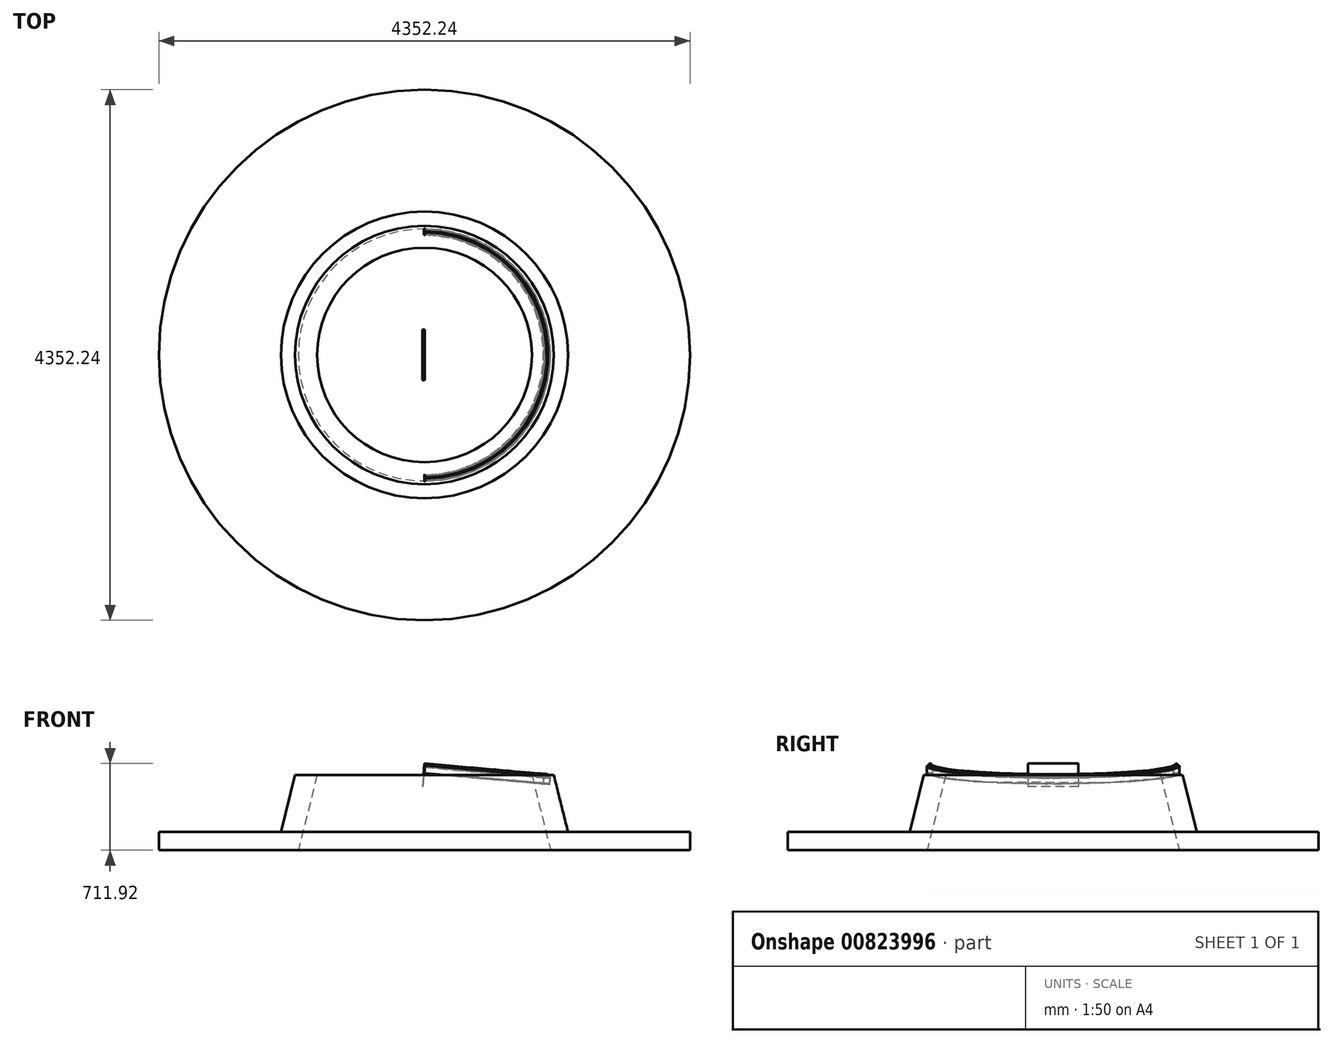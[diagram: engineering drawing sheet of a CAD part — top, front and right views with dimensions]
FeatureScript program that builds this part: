
annotation { "Feature Type Name" : "Feature", "Feature Type Description" : "" }
export const myFeature = defineFeature(function(context is Context, id is Id, definition is map)
    precondition{}
    {
        {
            var Q0;
            Q0=qCreatedBy(makeId("Front.planeOp"),FACE);
            var sketch = newSketch(context, id + "F0", { "sketchPlane" : qUnion([Q0])});
            skLineSegment(sketch, "E0", {"start": v(-2176.12, -465.74) * mm, "end": v(-1176.12, -465.74) * mm});
            skLineSegment(sketch, "E1", {"start": v(-1176.12, -465.74) * mm, "end": v(-1060, 0) * mm});
            skLineSegment(sketch, "E2", {"start": v(-1060, 0) * mm, "end": v(-880, 0) * mm});
            skLineSegment(sketch, "E3", {"start": v(-880, 0) * mm, "end": v(-1033.52, -615.74) * mm});
            skLineSegment(sketch, "E4", {"start": v(-2176.12, -465.74) * mm, "end": v(-2176.12, -615.74) * mm});
            skLineSegment(sketch, "E5", {"start": v(-2176.12, -615.74) * mm, "end": v(-1033.52, -615.74) * mm});
            skLineSegment(sketch, "E6", {"start": v(0, 0) * mm, "end": v(0, -606.45) * mm});
            skSolve(sketch);
        }
        {
            var Q0;
            Q0 = qSketchRegion(id + "F0", true);
            var Q1;
            Q1=sQuery(id+"F0.wireOp",EDGE,"E6");
            revolve(context, id + "F1", {"surfaceOperationType" : NewSurfaceOperationType.NEW, "entities" : qUnion([Q0]), "axis" : qUnion([Q1]), "revolveType" : RevolveType.FULL});
        }
        {
            var Q0;
            Q0=qCreatedBy(makeId("Right.planeOp"),FACE);
            var sketch = newSketch(context, id + "F2", { "sketchPlane" : qUnion([Q0])});
            skLineSegment(sketch, "E7.bottom", {"start": v(207.66, 95.39) * mm, "end": v(-207.66, 95.39) * mm});
            skLineSegment(sketch, "E7.top", {"start": v(207.66, -95.39) * mm, "end": v(-207.66, -95.39) * mm});
            skLineSegment(sketch, "E7.left", {"start": v(207.66, 95.39) * mm, "end": v(207.66, -95.39) * mm});
            skLineSegment(sketch, "E7.right", {"start": v(-207.66, 95.39) * mm, "end": v(-207.66, -95.39) * mm});
            skPoint(sketch, "E7.middle", {"position": v(0, 0) * mm});
            skSolve(sketch);
        }
        {
            var Q0;
            Q0=makeQuery(id+"F2.imprint","IMPRINT",FACE,{"disambiguationData":[TD([[makeQuery(id+"F2.imprint","IMPRINT",EDGE,{"derivedFrom":sQuery(id+"F2.wireOp",EDGE,"E7.bottom")}),1.0]])]});
            extrude(context, id + "F3", {"entities" : qUnion([Q0]), "depth" : 2 * mm, "offsetDistance" : 25 * mm});
        }
        {
            var Q0;
            Q0=makeQuery(id+"F3.opExtrude","SWEPT_BODY",BODY,{"disambiguationData":[OSD([sQuery(id+"F2.wireOp",EDGE,"E7.bottom"),sQuery(id+"F2.wireOp",EDGE,"E7.top"),sQuery(id+"F2.wireOp",EDGE,"E7.left"),sQuery(id+"F2.wireOp",EDGE,"E7.right")])]});
            var Q1;
            Q1=sQuery(id+"F2.wireOp",EDGE,"E7.bottom");
            transform(context, id + "F4", {"entities" : qUnion([Q0]), "transformType" : TransformType.ROTATION, "transformAxis" : qUnion([Q1]), "angle" : 5 * degree, "oppositeDirection" : true, "makeCopy" : false});
        }
        {
            var Q0;
            Q0=makeQuery(id+"F3.opExtrude","CAP_FACE",FACE,{"disambiguationData":[OSD([sQuery(id+"F2.wireOp",EDGE,"E7.bottom"),sQuery(id+"F2.wireOp",EDGE,"E7.top"),sQuery(id+"F2.wireOp",EDGE,"E7.left"),sQuery(id+"F2.wireOp",EDGE,"E7.right")])],"isStart":false});
            var sketch = newSketch(context, id + "F5", { "sketchPlane" : qUnion([Q0])});
            skArc(sketch, "E8", {"start": v(1012, 66) * mm, "mid": v(1012.7, 66.3) * mm, "end": v(1013, 67) * mm});
            skLineSegment(sketch, "E9", {"start": v(1013, 67) * mm, "end": v(1013, 78) * mm});
            skArc(sketch, "E10", {"start": v(1013, 78) * mm, "mid": v(1012.7, 78.7) * mm, "end": v(1012, 79) * mm});
            skLineSegment(sketch, "E11", {"start": v(1012, 79) * mm, "end": v(1008, 79) * mm});
            skArc(sketch, "E12", {"start": v(1008, 79) * mm, "mid": v(1007.3, 78.7) * mm, "end": v(1007, 78) * mm});
            skLineSegment(sketch, "E13", {"start": v(1007, 78) * mm, "end": v(1007, 67) * mm});
            skArc(sketch, "E14", {"start": v(1007, 67) * mm, "mid": v(1007.3, 66.3) * mm, "end": v(1008, 66) * mm});
            skLineSegment(sketch, "E15", {"start": v(1008, 66) * mm, "end": v(1012, 66) * mm});
            skLineSegment(sketch, "E16", {"start": v(986.6, 18.5) * mm, "end": v(995.5, 18.5) * mm});
            skLineSegment(sketch, "E17", {"start": v(995.5, 18.5) * mm, "end": v(995.5, 20.2) * mm});
            skLineSegment(sketch, "E18", {"start": v(995.5, 20.2) * mm, "end": v(997, 20.2) * mm});
            skLineSegment(sketch, "E19", {"start": v(997, 20.2) * mm, "end": v(997, 18.5) * mm});
            skLineSegment(sketch, "E20", {"start": v(997, 18.5) * mm, "end": v(1023, 18.5) * mm});
            skLineSegment(sketch, "E21", {"start": v(1023, 18.5) * mm, "end": v(1023, 20.2) * mm});
            skLineSegment(sketch, "E22", {"start": v(1023, 20.2) * mm, "end": v(1024.5, 20.2) * mm});
            skLineSegment(sketch, "E23", {"start": v(1024.5, 20.2) * mm, "end": v(1024.5, 18.5) * mm});
            skLineSegment(sketch, "E24", {"start": v(1024.5, 18.5) * mm, "end": v(1033.4, 18.5) * mm});
            skArc(sketch, "E25", {"start": v(1033.4, 18.5) * mm, "mid": v(1033.75, 18.65) * mm, "end": v(1033.9, 19) * mm});
            skLineSegment(sketch, "E26", {"start": v(1033.9, 19) * mm, "end": v(1033.9, 63.2) * mm});
            skArc(sketch, "E27", {"start": v(1033.9, 63.2) * mm, "mid": v(1033.75, 63.55) * mm, "end": v(1033.4, 63.7) * mm});
            skLineSegment(sketch, "E28", {"start": v(1033.4, 63.7) * mm, "end": v(986.6, 63.7) * mm});
            skArc(sketch, "E29", {"start": v(986.6, 63.7) * mm, "mid": v(986.25, 63.55) * mm, "end": v(986.1, 63.2) * mm});
            skLineSegment(sketch, "E30", {"start": v(986.1, 63.2) * mm, "end": v(986.1, 19) * mm});
            skArc(sketch, "E31", {"start": v(986.1, 19) * mm, "mid": v(986.25, 18.65) * mm, "end": v(986.6, 18.5) * mm});
            skArc(sketch, "E32", {"start": v(987.2, 67.35) * mm, "mid": v(988.85, 66) * mm, "end": v(990.31, 67.56) * mm});
            skLineSegment(sketch, "E33", {"start": v(990.3, 67.56) * mm, "end": v(990.3, 68.02) * mm});
            skArc(sketch, "E34", {"start": v(990.3, 68.02) * mm, "mid": v(990.35, 68.17) * mm, "end": v(990.46, 68.28) * mm});
            skLineSegment(sketch, "E35", {"start": v(990.46, 68.28) * mm, "end": v(990.6, 68.37) * mm});
            skArc(sketch, "E36", {"start": v(990.61, 68.37) * mm, "mid": v(990.7, 68.54) * mm, "end": v(990.61, 68.71) * mm});
            skLineSegment(sketch, "E37", {"start": v(990.6, 68.71) * mm, "end": v(990.46, 68.8) * mm});
            skArc(sketch, "E38", {"start": v(990.46, 68.8) * mm, "mid": v(990.35, 68.91) * mm, "end": v(990.3, 69.06) * mm});
            skLineSegment(sketch, "E39", {"start": v(990.3, 69.06) * mm, "end": v(990.3, 69.42) * mm});
            skArc(sketch, "E40", {"start": v(990.3, 69.42) * mm, "mid": v(990.35, 69.57) * mm, "end": v(990.46, 69.68) * mm});
            skLineSegment(sketch, "E41", {"start": v(990.46, 69.68) * mm, "end": v(990.6, 69.77) * mm});
            skArc(sketch, "E42", {"start": v(990.61, 69.77) * mm, "mid": v(990.7, 69.94) * mm, "end": v(990.61, 70.11) * mm});
            skLineSegment(sketch, "E43", {"start": v(990.6, 70.11) * mm, "end": v(990.46, 70.2) * mm});
            skArc(sketch, "E44", {"start": v(990.46, 70.2) * mm, "mid": v(990.45, 70.2) * mm, "end": v(990.45, 70.2) * mm});
            skLineSegment(sketch, "E45", {"start": v(990.45, 70.2) * mm, "end": v(991.3, 71.07) * mm});
            skLineSegment(sketch, "E46", {"start": v(991.3, 71.07) * mm, "end": v(991.3, 72) * mm});
            skLineSegment(sketch, "E47", {"start": v(991.3, 72) * mm, "end": v(990.3, 72) * mm});
            skLineSegment(sketch, "E48", {"start": v(990.3, 72) * mm, "end": v(990.3, 72.22) * mm});
            skArc(sketch, "E49", {"start": v(990.3, 72.22) * mm, "mid": v(990.35, 72.37) * mm, "end": v(990.46, 72.48) * mm});
            skLineSegment(sketch, "E50", {"start": v(990.46, 72.48) * mm, "end": v(990.6, 72.57) * mm});
            skArc(sketch, "E51", {"start": v(990.61, 72.57) * mm, "mid": v(990.7, 72.74) * mm, "end": v(990.61, 72.91) * mm});
            skLineSegment(sketch, "E52", {"start": v(990.6, 72.91) * mm, "end": v(990.46, 73) * mm});
            skArc(sketch, "E53", {"start": v(990.46, 73) * mm, "mid": v(990.35, 73.11) * mm, "end": v(990.3, 73.26) * mm});
            skLineSegment(sketch, "E54", {"start": v(990.3, 73.26) * mm, "end": v(990.3, 73.62) * mm});
            skArc(sketch, "E55", {"start": v(990.3, 73.62) * mm, "mid": v(990.35, 73.77) * mm, "end": v(990.46, 73.88) * mm});
            skLineSegment(sketch, "E56", {"start": v(990.46, 73.88) * mm, "end": v(990.6, 73.97) * mm});
            skArc(sketch, "E57", {"start": v(990.61, 73.97) * mm, "mid": v(990.7, 74.14) * mm, "end": v(990.61, 74.31) * mm});
            skLineSegment(sketch, "E58", {"start": v(990.6, 74.31) * mm, "end": v(990.46, 74.4) * mm});
            skArc(sketch, "E59", {"start": v(990.46, 74.4) * mm, "mid": v(990.35, 74.51) * mm, "end": v(990.3, 74.66) * mm});
            skLineSegment(sketch, "E60", {"start": v(990.3, 74.66) * mm, "end": v(990.3, 75.02) * mm});
            skArc(sketch, "E61", {"start": v(990.3, 75.02) * mm, "mid": v(990.35, 75.17) * mm, "end": v(990.46, 75.28) * mm});
            skLineSegment(sketch, "E62", {"start": v(990.46, 75.28) * mm, "end": v(990.6, 75.37) * mm});
            skArc(sketch, "E63", {"start": v(990.61, 75.37) * mm, "mid": v(990.7, 75.54) * mm, "end": v(990.61, 75.71) * mm});
            skLineSegment(sketch, "E64", {"start": v(990.6, 75.71) * mm, "end": v(990.46, 75.8) * mm});
            skArc(sketch, "E65", {"start": v(990.46, 75.8) * mm, "mid": v(990.35, 75.91) * mm, "end": v(990.31, 76.07) * mm});
            skLineSegment(sketch, "E66", {"start": v(990.31, 76.07) * mm, "end": v(991.3, 77.07) * mm});
            skLineSegment(sketch, "E67", {"start": v(991.3, 77.07) * mm, "end": v(991.3, 78) * mm});
            skLineSegment(sketch, "E68", {"start": v(991.3, 78) * mm, "end": v(990.3, 78) * mm});
            skLineSegment(sketch, "E69", {"start": v(990.3, 78) * mm, "end": v(990.3, 78.5) * mm});
            skLineSegment(sketch, "E70", {"start": v(990.3, 78.5) * mm, "end": v(990.8, 79) * mm});
            skLineSegment(sketch, "E71", {"start": v(990.8, 79) * mm, "end": v(993.5, 79) * mm});
            skLineSegment(sketch, "E72", {"start": v(993.5, 79) * mm, "end": v(993.5, 67) * mm});
            skArc(sketch, "E73", {"start": v(993.5, 67) * mm, "mid": v(993.8, 66.3) * mm, "end": v(994.5, 66) * mm});
            skLineSegment(sketch, "E74", {"start": v(994.5, 66) * mm, "end": v(998.95, 66) * mm});
            skLineSegment(sketch, "E75", {"start": v(998.95, 66) * mm, "end": v(999.25, 65.7) * mm});
            skLineSegment(sketch, "E76", {"start": v(999.25, 65.7) * mm, "end": v(999.55, 66) * mm});
            skLineSegment(sketch, "E77", {"start": v(999.55, 66) * mm, "end": v(1004, 66) * mm});
            skArc(sketch, "E78", {"start": v(1004, 66) * mm, "mid": v(1004.7, 66.3) * mm, "end": v(1005, 67) * mm});
            skLineSegment(sketch, "E79", {"start": v(1005, 67) * mm, "end": v(1005, 96) * mm});
            skLineSegment(sketch, "E80", {"start": v(1005, 96) * mm, "end": v(1006.7, 96) * mm});
            skLineSegment(sketch, "E81", {"start": v(1006.7, 96) * mm, "end": v(1007.88, 94.82) * mm});
            skArc(sketch, "E82", {"start": v(1007.88, 94.82) * mm, "mid": v(1007.88, 94.61) * mm, "end": v(1007.75, 94.46) * mm});
            skLineSegment(sketch, "E83", {"start": v(1007.75, 94.46) * mm, "end": v(1007.6, 94.37) * mm});
            skArc(sketch, "E84", {"start": v(1007.6, 94.37) * mm, "mid": v(1007.5, 94.2) * mm, "end": v(1007.6, 94.03) * mm});
            skLineSegment(sketch, "E85", {"start": v(1007.6, 94.03) * mm, "end": v(1007.75, 93.94) * mm});
            skArc(sketch, "E86", {"start": v(1007.75, 93.94) * mm, "mid": v(1007.86, 93.83) * mm, "end": v(1007.9, 93.68) * mm});
            skLineSegment(sketch, "E87", {"start": v(1007.9, 93.68) * mm, "end": v(1007.9, 92.92) * mm});
            skArc(sketch, "E88", {"start": v(1007.9, 92.92) * mm, "mid": v(1007.86, 92.77) * mm, "end": v(1007.75, 92.66) * mm});
            skLineSegment(sketch, "E89", {"start": v(1007.75, 92.66) * mm, "end": v(1007.6, 92.57) * mm});
            skArc(sketch, "E90", {"start": v(1007.6, 92.57) * mm, "mid": v(1007.5, 92.4) * mm, "end": v(1007.6, 92.23) * mm});
            skLineSegment(sketch, "E91", {"start": v(1007.6, 92.23) * mm, "end": v(1007.75, 92.14) * mm});
            skArc(sketch, "E92", {"start": v(1007.75, 92.14) * mm, "mid": v(1007.86, 92.03) * mm, "end": v(1007.9, 91.88) * mm});
            skLineSegment(sketch, "E93", {"start": v(1007.9, 91.88) * mm, "end": v(1007.9, 91.12) * mm});
            skArc(sketch, "E94", {"start": v(1007.9, 91.12) * mm, "mid": v(1007.86, 90.97) * mm, "end": v(1007.75, 90.86) * mm});
            skLineSegment(sketch, "E95", {"start": v(1007.75, 90.86) * mm, "end": v(1007.6, 90.77) * mm});
            skArc(sketch, "E96", {"start": v(1007.6, 90.77) * mm, "mid": v(1007.5, 90.6) * mm, "end": v(1007.6, 90.43) * mm});
            skLineSegment(sketch, "E97", {"start": v(1007.6, 90.43) * mm, "end": v(1007.75, 90.34) * mm});
            skArc(sketch, "E98", {"start": v(1007.75, 90.34) * mm, "mid": v(1007.86, 90.23) * mm, "end": v(1007.9, 90.08) * mm});
            skLineSegment(sketch, "E99", {"start": v(1007.9, 90.08) * mm, "end": v(1007.9, 89.32) * mm});
            skArc(sketch, "E100", {"start": v(1007.9, 89.32) * mm, "mid": v(1007.86, 89.17) * mm, "end": v(1007.75, 89.06) * mm});
            skLineSegment(sketch, "E101", {"start": v(1007.75, 89.06) * mm, "end": v(1007.6, 88.97) * mm});
            skArc(sketch, "E102", {"start": v(1007.6, 88.97) * mm, "mid": v(1007.5, 88.8) * mm, "end": v(1007.6, 88.63) * mm});
            skLineSegment(sketch, "E103", {"start": v(1007.6, 88.63) * mm, "end": v(1007.75, 88.54) * mm});
            skArc(sketch, "E104", {"start": v(1007.75, 88.54) * mm, "mid": v(1007.86, 88.43) * mm, "end": v(1007.9, 88.28) * mm});
            skLineSegment(sketch, "E105", {"start": v(1007.9, 88.28) * mm, "end": v(1007.9, 87.52) * mm});
            skArc(sketch, "E106", {"start": v(1007.9, 87.52) * mm, "mid": v(1007.86, 87.37) * mm, "end": v(1007.75, 87.26) * mm});
            skLineSegment(sketch, "E107", {"start": v(1007.75, 87.26) * mm, "end": v(1007.6, 87.17) * mm});
            skArc(sketch, "E108", {"start": v(1007.6, 87.17) * mm, "mid": v(1007.5, 87) * mm, "end": v(1007.6, 86.83) * mm});
            skLineSegment(sketch, "E109", {"start": v(1007.6, 86.83) * mm, "end": v(1007.75, 86.74) * mm});
            skArc(sketch, "E110", {"start": v(1007.75, 86.74) * mm, "mid": v(1007.86, 86.63) * mm, "end": v(1007.9, 86.48) * mm});
            skLineSegment(sketch, "E111", {"start": v(1007.9, 86.48) * mm, "end": v(1007.9, 85.72) * mm});
            skArc(sketch, "E112", {"start": v(1007.9, 85.72) * mm, "mid": v(1007.86, 85.57) * mm, "end": v(1007.75, 85.46) * mm});
            skLineSegment(sketch, "E113", {"start": v(1007.75, 85.46) * mm, "end": v(1007.6, 85.37) * mm});
            skArc(sketch, "E114", {"start": v(1007.6, 85.37) * mm, "mid": v(1007.5, 85.2) * mm, "end": v(1007.6, 85.03) * mm});
            skLineSegment(sketch, "E115", {"start": v(1007.6, 85.03) * mm, "end": v(1007.75, 84.94) * mm});
            skArc(sketch, "E116", {"start": v(1007.75, 84.94) * mm, "mid": v(1007.86, 84.83) * mm, "end": v(1007.9, 84.68) * mm});
            skLineSegment(sketch, "E117", {"start": v(1007.9, 84.68) * mm, "end": v(1007.9, 83.1) * mm});
            skArc(sketch, "E118", {"start": v(1007.9, 83.1) * mm, "mid": v(1008.34, 82.04) * mm, "end": v(1009.4, 81.6) * mm});
            skLineSegment(sketch, "E119", {"start": v(1009.4, 81.6) * mm, "end": v(1010.6, 81.6) * mm});
            skArc(sketch, "E120", {"start": v(1010.6, 81.6) * mm, "mid": v(1011.66, 82.04) * mm, "end": v(1012.1, 83.1) * mm});
            skLineSegment(sketch, "E121", {"start": v(1012.1, 83.1) * mm, "end": v(1012.1, 83.78) * mm});
            skArc(sketch, "E122", {"start": v(1012.1, 83.78) * mm, "mid": v(1012.14, 83.93) * mm, "end": v(1012.25, 84.04) * mm});
            skLineSegment(sketch, "E123", {"start": v(1012.25, 84.04) * mm, "end": v(1012.4, 84.13) * mm});
            skArc(sketch, "E124", {"start": v(1012.4, 84.13) * mm, "mid": v(1012.5, 84.3) * mm, "end": v(1012.4, 84.47) * mm});
            skLineSegment(sketch, "E125", {"start": v(1012.4, 84.47) * mm, "end": v(1012.25, 84.56) * mm});
            skArc(sketch, "E126", {"start": v(1012.25, 84.56) * mm, "mid": v(1012.14, 84.67) * mm, "end": v(1012.1, 84.82) * mm});
            skLineSegment(sketch, "E127", {"start": v(1012.1, 84.82) * mm, "end": v(1012.1, 85.58) * mm});
            skArc(sketch, "E128", {"start": v(1012.1, 85.58) * mm, "mid": v(1012.14, 85.73) * mm, "end": v(1012.25, 85.84) * mm});
            skLineSegment(sketch, "E129", {"start": v(1012.25, 85.84) * mm, "end": v(1012.4, 85.93) * mm});
            skArc(sketch, "E130", {"start": v(1012.4, 85.93) * mm, "mid": v(1012.5, 86.1) * mm, "end": v(1012.4, 86.27) * mm});
            skLineSegment(sketch, "E131", {"start": v(1012.4, 86.27) * mm, "end": v(1012.25, 86.36) * mm});
            skArc(sketch, "E132", {"start": v(1012.25, 86.36) * mm, "mid": v(1012.14, 86.47) * mm, "end": v(1012.1, 86.62) * mm});
            skLineSegment(sketch, "E133", {"start": v(1012.1, 86.62) * mm, "end": v(1012.1, 87.38) * mm});
            skArc(sketch, "E134", {"start": v(1012.1, 87.38) * mm, "mid": v(1012.14, 87.53) * mm, "end": v(1012.25, 87.64) * mm});
            skLineSegment(sketch, "E135", {"start": v(1012.25, 87.64) * mm, "end": v(1012.4, 87.73) * mm});
            skArc(sketch, "E136", {"start": v(1012.4, 87.73) * mm, "mid": v(1012.5, 87.9) * mm, "end": v(1012.4, 88.07) * mm});
            skLineSegment(sketch, "E137", {"start": v(1012.4, 88.07) * mm, "end": v(1012.25, 88.16) * mm});
            skArc(sketch, "E138", {"start": v(1012.25, 88.16) * mm, "mid": v(1012.14, 88.27) * mm, "end": v(1012.1, 88.42) * mm});
            skLineSegment(sketch, "E139", {"start": v(1012.1, 88.42) * mm, "end": v(1012.1, 89.18) * mm});
            skArc(sketch, "E140", {"start": v(1012.1, 89.18) * mm, "mid": v(1012.14, 89.33) * mm, "end": v(1012.25, 89.44) * mm});
            skLineSegment(sketch, "E141", {"start": v(1012.25, 89.44) * mm, "end": v(1012.4, 89.53) * mm});
            skArc(sketch, "E142", {"start": v(1012.4, 89.53) * mm, "mid": v(1012.5, 89.7) * mm, "end": v(1012.4, 89.87) * mm});
            skLineSegment(sketch, "E143", {"start": v(1012.4, 89.87) * mm, "end": v(1012.25, 89.96) * mm});
            skArc(sketch, "E144", {"start": v(1012.25, 89.96) * mm, "mid": v(1012.14, 90.07) * mm, "end": v(1012.1, 90.22) * mm});
            skLineSegment(sketch, "E145", {"start": v(1012.1, 90.22) * mm, "end": v(1012.1, 90.98) * mm});
            skArc(sketch, "E146", {"start": v(1012.1, 90.98) * mm, "mid": v(1012.14, 91.13) * mm, "end": v(1012.25, 91.24) * mm});
            skLineSegment(sketch, "E147", {"start": v(1012.25, 91.24) * mm, "end": v(1012.4, 91.33) * mm});
            skArc(sketch, "E148", {"start": v(1012.4, 91.33) * mm, "mid": v(1012.5, 91.5) * mm, "end": v(1012.4, 91.67) * mm});
            skLineSegment(sketch, "E149", {"start": v(1012.4, 91.67) * mm, "end": v(1012.25, 91.76) * mm});
            skArc(sketch, "E150", {"start": v(1012.25, 91.76) * mm, "mid": v(1012.14, 91.87) * mm, "end": v(1012.1, 92.02) * mm});
            skLineSegment(sketch, "E151", {"start": v(1012.1, 92.02) * mm, "end": v(1012.1, 92.78) * mm});
            skArc(sketch, "E152", {"start": v(1012.1, 92.78) * mm, "mid": v(1012.14, 92.93) * mm, "end": v(1012.25, 93.04) * mm});
            skLineSegment(sketch, "E153", {"start": v(1012.25, 93.04) * mm, "end": v(1012.4, 93.13) * mm});
            skArc(sketch, "E154", {"start": v(1012.4, 93.13) * mm, "mid": v(1012.5, 93.3) * mm, "end": v(1012.4, 93.47) * mm});
            skLineSegment(sketch, "E155", {"start": v(1012.4, 93.47) * mm, "end": v(1012.25, 93.56) * mm});
            skArc(sketch, "E156", {"start": v(1012.25, 93.56) * mm, "mid": v(1012.14, 93.67) * mm, "end": v(1012.1, 93.82) * mm});
            skLineSegment(sketch, "E157", {"start": v(1012.1, 93.82) * mm, "end": v(1012.1, 94.8) * mm});
            skLineSegment(sketch, "E158", {"start": v(1012.1, 94.8) * mm, "end": v(1013.3, 96) * mm});
            skLineSegment(sketch, "E159", {"start": v(1013.3, 96) * mm, "end": v(1015, 96) * mm});
            skLineSegment(sketch, "E160", {"start": v(1015, 96) * mm, "end": v(1015, 67) * mm});
            skArc(sketch, "E161", {"start": v(1015, 67) * mm, "mid": v(1015.3, 66.3) * mm, "end": v(1016, 66) * mm});
            skLineSegment(sketch, "E162", {"start": v(1016, 66) * mm, "end": v(1020.45, 66) * mm});
            skLineSegment(sketch, "E163", {"start": v(1020.45, 66) * mm, "end": v(1020.75, 65.7) * mm});
            skLineSegment(sketch, "E164", {"start": v(1020.75, 65.7) * mm, "end": v(1021.05, 66) * mm});
            skLineSegment(sketch, "E165", {"start": v(1021.05, 66) * mm, "end": v(1025.5, 66) * mm});
            skArc(sketch, "E166", {"start": v(1025.5, 66) * mm, "mid": v(1026.2, 66.3) * mm, "end": v(1026.5, 67) * mm});
            skLineSegment(sketch, "E167", {"start": v(1026.5, 67) * mm, "end": v(1026.5, 79) * mm});
            skLineSegment(sketch, "E168", {"start": v(1026.5, 79) * mm, "end": v(1029.19, 79) * mm});
            skLineSegment(sketch, "E169", {"start": v(1029.19, 79) * mm, "end": v(1029.69, 78.5) * mm});
            skLineSegment(sketch, "E170", {"start": v(1029.69, 78.5) * mm, "end": v(1029.69, 78) * mm});
            skLineSegment(sketch, "E171", {"start": v(1029.69, 78) * mm, "end": v(1028.69, 78) * mm});
            skLineSegment(sketch, "E172", {"start": v(1028.69, 78) * mm, "end": v(1028.69, 77.07) * mm});
            skLineSegment(sketch, "E173", {"start": v(1028.69, 77.07) * mm, "end": v(1029.69, 76.07) * mm});
            skArc(sketch, "E174", {"start": v(1029.69, 76.07) * mm, "mid": v(1029.65, 75.91) * mm, "end": v(1029.54, 75.8) * mm});
            skLineSegment(sketch, "E175", {"start": v(1029.54, 75.8) * mm, "end": v(1029.39, 75.71) * mm});
            skArc(sketch, "E176", {"start": v(1029.39, 75.71) * mm, "mid": v(1029.29, 75.54) * mm, "end": v(1029.39, 75.37) * mm});
            skLineSegment(sketch, "E177", {"start": v(1029.39, 75.37) * mm, "end": v(1029.54, 75.28) * mm});
            skArc(sketch, "E178", {"start": v(1029.54, 75.28) * mm, "mid": v(1029.65, 75.17) * mm, "end": v(1029.69, 75.02) * mm});
            skLineSegment(sketch, "E179", {"start": v(1029.69, 75.02) * mm, "end": v(1029.69, 74.66) * mm});
            skArc(sketch, "E180", {"start": v(1029.69, 74.66) * mm, "mid": v(1029.65, 74.51) * mm, "end": v(1029.54, 74.4) * mm});
            skLineSegment(sketch, "E181", {"start": v(1029.54, 74.4) * mm, "end": v(1029.39, 74.31) * mm});
            skArc(sketch, "E182", {"start": v(1029.39, 74.31) * mm, "mid": v(1029.29, 74.14) * mm, "end": v(1029.39, 73.97) * mm});
            skLineSegment(sketch, "E183", {"start": v(1029.39, 73.97) * mm, "end": v(1029.54, 73.88) * mm});
            skArc(sketch, "E184", {"start": v(1029.54, 73.88) * mm, "mid": v(1029.65, 73.77) * mm, "end": v(1029.69, 73.62) * mm});
            skLineSegment(sketch, "E185", {"start": v(1029.69, 73.62) * mm, "end": v(1029.69, 73.26) * mm});
            skArc(sketch, "E186", {"start": v(1029.69, 73.26) * mm, "mid": v(1029.65, 73.11) * mm, "end": v(1029.54, 73) * mm});
            skLineSegment(sketch, "E187", {"start": v(1029.54, 73) * mm, "end": v(1029.39, 72.91) * mm});
            skArc(sketch, "E188", {"start": v(1029.39, 72.91) * mm, "mid": v(1029.29, 72.74) * mm, "end": v(1029.39, 72.57) * mm});
            skLineSegment(sketch, "E189", {"start": v(1029.39, 72.57) * mm, "end": v(1029.54, 72.48) * mm});
            skArc(sketch, "E190", {"start": v(1029.54, 72.48) * mm, "mid": v(1029.65, 72.37) * mm, "end": v(1029.69, 72.22) * mm});
            skLineSegment(sketch, "E191", {"start": v(1029.69, 72.22) * mm, "end": v(1029.69, 72) * mm});
            skLineSegment(sketch, "E192", {"start": v(1029.69, 72) * mm, "end": v(1028.69, 72) * mm});
            skLineSegment(sketch, "E193", {"start": v(1028.69, 72) * mm, "end": v(1028.69, 71.07) * mm});
            skLineSegment(sketch, "E194", {"start": v(1028.69, 71.07) * mm, "end": v(1029.55, 70.2) * mm});
            skArc(sketch, "E195", {"start": v(1029.55, 70.2) * mm, "mid": v(1029.55, 70.2) * mm, "end": v(1029.54, 70.2) * mm});
            skLineSegment(sketch, "E196", {"start": v(1029.54, 70.2) * mm, "end": v(1029.39, 70.11) * mm});
            skArc(sketch, "E197", {"start": v(1029.39, 70.11) * mm, "mid": v(1029.29, 69.94) * mm, "end": v(1029.39, 69.77) * mm});
            skLineSegment(sketch, "E198", {"start": v(1029.39, 69.77) * mm, "end": v(1029.54, 69.68) * mm});
            skArc(sketch, "E199", {"start": v(1029.54, 69.68) * mm, "mid": v(1029.65, 69.57) * mm, "end": v(1029.69, 69.42) * mm});
            skLineSegment(sketch, "E200", {"start": v(1029.69, 69.42) * mm, "end": v(1029.69, 69.06) * mm});
            skArc(sketch, "E201", {"start": v(1029.69, 69.06) * mm, "mid": v(1029.65, 68.91) * mm, "end": v(1029.54, 68.8) * mm});
            skLineSegment(sketch, "E202", {"start": v(1029.54, 68.8) * mm, "end": v(1029.39, 68.71) * mm});
            skArc(sketch, "E203", {"start": v(1029.39, 68.71) * mm, "mid": v(1029.29, 68.54) * mm, "end": v(1029.39, 68.37) * mm});
            skLineSegment(sketch, "E204", {"start": v(1029.39, 68.37) * mm, "end": v(1029.54, 68.28) * mm});
            skArc(sketch, "E205", {"start": v(1029.54, 68.28) * mm, "mid": v(1029.65, 68.17) * mm, "end": v(1029.69, 68.02) * mm});
            skLineSegment(sketch, "E206", {"start": v(1029.69, 68.02) * mm, "end": v(1029.69, 67.56) * mm});
            skArc(sketch, "E207", {"start": v(1029.7, 67.56) * mm, "mid": v(1031.15, 66) * mm, "end": v(1032.8, 67.35) * mm});
            skArc(sketch, "E208", {"start": v(1032.8, 67.35) * mm, "mid": v(1032.84, 67.48) * mm, "end": v(1032.94, 67.57) * mm});
            skLineSegment(sketch, "E209", {"start": v(1032.94, 67.57) * mm, "end": v(1033.1, 67.67) * mm});
            skArc(sketch, "E210", {"start": v(1033.11, 67.67) * mm, "mid": v(1033.2, 67.84) * mm, "end": v(1033.11, 68.01) * mm});
            skLineSegment(sketch, "E211", {"start": v(1033.1, 68.01) * mm, "end": v(1032.96, 68.1) * mm});
            skArc(sketch, "E212", {"start": v(1032.96, 68.1) * mm, "mid": v(1032.85, 68.21) * mm, "end": v(1032.8, 68.36) * mm});
            skLineSegment(sketch, "E213", {"start": v(1032.8, 68.36) * mm, "end": v(1032.8, 68.72) * mm});
            skArc(sketch, "E214", {"start": v(1032.8, 68.72) * mm, "mid": v(1032.85, 68.87) * mm, "end": v(1032.96, 68.98) * mm});
            skLineSegment(sketch, "E215", {"start": v(1032.96, 68.98) * mm, "end": v(1033.1, 69.07) * mm});
            skArc(sketch, "E216", {"start": v(1033.11, 69.07) * mm, "mid": v(1033.2, 69.24) * mm, "end": v(1033.11, 69.41) * mm});
            skLineSegment(sketch, "E217", {"start": v(1033.1, 69.41) * mm, "end": v(1032.96, 69.5) * mm});
            skArc(sketch, "E218", {"start": v(1032.96, 69.5) * mm, "mid": v(1032.85, 69.61) * mm, "end": v(1032.8, 69.76) * mm});
            skLineSegment(sketch, "E219", {"start": v(1032.8, 69.76) * mm, "end": v(1032.8, 70.07) * mm});
            skLineSegment(sketch, "E220", {"start": v(1032.8, 70.07) * mm, "end": v(1033.81, 71.07) * mm});
            skLineSegment(sketch, "E221", {"start": v(1033.8, 71.07) * mm, "end": v(1033.8, 72) * mm});
            skLineSegment(sketch, "E222", {"start": v(1033.8, 72) * mm, "end": v(1032.8, 72) * mm});
            skLineSegment(sketch, "E223", {"start": v(1032.8, 72) * mm, "end": v(1032.8, 72.92) * mm});
            skArc(sketch, "E224", {"start": v(1032.8, 72.92) * mm, "mid": v(1032.85, 73.07) * mm, "end": v(1032.96, 73.18) * mm});
            skLineSegment(sketch, "E225", {"start": v(1032.96, 73.18) * mm, "end": v(1033.1, 73.27) * mm});
            skArc(sketch, "E226", {"start": v(1033.11, 73.27) * mm, "mid": v(1033.2, 73.44) * mm, "end": v(1033.11, 73.61) * mm});
            skLineSegment(sketch, "E227", {"start": v(1033.1, 73.61) * mm, "end": v(1032.96, 73.7) * mm});
            skArc(sketch, "E228", {"start": v(1032.96, 73.7) * mm, "mid": v(1032.85, 73.81) * mm, "end": v(1032.8, 73.96) * mm});
            skLineSegment(sketch, "E229", {"start": v(1032.8, 73.96) * mm, "end": v(1032.8, 74.32) * mm});
            skArc(sketch, "E230", {"start": v(1032.8, 74.32) * mm, "mid": v(1032.85, 74.47) * mm, "end": v(1032.96, 74.58) * mm});
            skLineSegment(sketch, "E231", {"start": v(1032.96, 74.58) * mm, "end": v(1033.1, 74.67) * mm});
            skArc(sketch, "E232", {"start": v(1033.11, 74.67) * mm, "mid": v(1033.2, 74.84) * mm, "end": v(1033.11, 75.01) * mm});
            skLineSegment(sketch, "E233", {"start": v(1033.1, 75.01) * mm, "end": v(1032.96, 75.1) * mm});
            skArc(sketch, "E234", {"start": v(1032.96, 75.1) * mm, "mid": v(1032.85, 75.21) * mm, "end": v(1032.8, 75.36) * mm});
            skLineSegment(sketch, "E235", {"start": v(1032.8, 75.36) * mm, "end": v(1032.8, 76.07) * mm});
            skLineSegment(sketch, "E236", {"start": v(1032.8, 76.07) * mm, "end": v(1033.81, 77.07) * mm});
            skLineSegment(sketch, "E237", {"start": v(1033.8, 77.07) * mm, "end": v(1033.8, 78) * mm});
            skLineSegment(sketch, "E238", {"start": v(1033.8, 78) * mm, "end": v(1032.8, 78) * mm});
            skLineSegment(sketch, "E239", {"start": v(1032.8, 78) * mm, "end": v(1032.8, 78.5) * mm});
            skLineSegment(sketch, "E240", {"start": v(1032.8, 78.5) * mm, "end": v(1033.3, 79) * mm});
            skLineSegment(sketch, "E241", {"start": v(1033.3, 79) * mm, "end": v(1036, 79) * mm});
            skLineSegment(sketch, "E242", {"start": v(1036, 79) * mm, "end": v(1036, 14.5) * mm});
            skArc(sketch, "E243", {"start": v(1036, 14.5) * mm, "mid": v(1035.85, 14.15) * mm, "end": v(1035.5, 14) * mm});
            skLineSegment(sketch, "E244", {"start": v(1035.5, 14) * mm, "end": v(984.5, 14) * mm});
            skArc(sketch, "E245", {"start": v(984.5, 14) * mm, "mid": v(984.15, 14.15) * mm, "end": v(984, 14.5) * mm});
            skLineSegment(sketch, "E246", {"start": v(984, 14.5) * mm, "end": v(984, 79) * mm});
            skLineSegment(sketch, "E247", {"start": v(984, 79) * mm, "end": v(986.69, 79) * mm});
            skLineSegment(sketch, "E248", {"start": v(986.69, 79) * mm, "end": v(987.19, 78.5) * mm});
            skLineSegment(sketch, "E249", {"start": v(987.19, 78.5) * mm, "end": v(987.19, 78) * mm});
            skLineSegment(sketch, "E250", {"start": v(987.19, 78) * mm, "end": v(986.19, 78) * mm});
            skLineSegment(sketch, "E251", {"start": v(986.19, 78) * mm, "end": v(986.19, 77.07) * mm});
            skLineSegment(sketch, "E252", {"start": v(986.19, 77.07) * mm, "end": v(987.19, 76.07) * mm});
            skLineSegment(sketch, "E253", {"start": v(987.19, 76.07) * mm, "end": v(987.19, 75.36) * mm});
            skArc(sketch, "E254", {"start": v(987.19, 75.36) * mm, "mid": v(987.15, 75.21) * mm, "end": v(987.04, 75.1) * mm});
            skLineSegment(sketch, "E255", {"start": v(987.04, 75.1) * mm, "end": v(986.89, 75.01) * mm});
            skArc(sketch, "E256", {"start": v(986.89, 75.01) * mm, "mid": v(986.79, 74.84) * mm, "end": v(986.89, 74.67) * mm});
            skLineSegment(sketch, "E257", {"start": v(986.89, 74.67) * mm, "end": v(987.04, 74.58) * mm});
            skArc(sketch, "E258", {"start": v(987.04, 74.58) * mm, "mid": v(987.15, 74.47) * mm, "end": v(987.19, 74.32) * mm});
            skLineSegment(sketch, "E259", {"start": v(987.19, 74.32) * mm, "end": v(987.19, 73.96) * mm});
            skArc(sketch, "E260", {"start": v(987.19, 73.96) * mm, "mid": v(987.15, 73.81) * mm, "end": v(987.04, 73.7) * mm});
            skLineSegment(sketch, "E261", {"start": v(987.04, 73.7) * mm, "end": v(986.89, 73.61) * mm});
            skArc(sketch, "E262", {"start": v(986.89, 73.61) * mm, "mid": v(986.79, 73.44) * mm, "end": v(986.89, 73.27) * mm});
            skLineSegment(sketch, "E263", {"start": v(986.89, 73.27) * mm, "end": v(987.04, 73.18) * mm});
            skArc(sketch, "E264", {"start": v(987.04, 73.18) * mm, "mid": v(987.15, 73.07) * mm, "end": v(987.19, 72.92) * mm});
            skLineSegment(sketch, "E265", {"start": v(987.19, 72.92) * mm, "end": v(987.19, 72) * mm});
            skLineSegment(sketch, "E266", {"start": v(987.19, 72) * mm, "end": v(986.19, 72) * mm});
            skLineSegment(sketch, "E267", {"start": v(986.19, 72) * mm, "end": v(986.19, 71.07) * mm});
            skLineSegment(sketch, "E268", {"start": v(986.19, 71.07) * mm, "end": v(987.19, 70.07) * mm});
            skLineSegment(sketch, "E269", {"start": v(987.19, 70.07) * mm, "end": v(987.19, 69.76) * mm});
            skArc(sketch, "E270", {"start": v(987.19, 69.76) * mm, "mid": v(987.15, 69.61) * mm, "end": v(987.04, 69.5) * mm});
            skLineSegment(sketch, "E271", {"start": v(987.04, 69.5) * mm, "end": v(986.89, 69.41) * mm});
            skArc(sketch, "E272", {"start": v(986.89, 69.41) * mm, "mid": v(986.79, 69.24) * mm, "end": v(986.89, 69.07) * mm});
            skLineSegment(sketch, "E273", {"start": v(986.89, 69.07) * mm, "end": v(987.04, 68.98) * mm});
            skArc(sketch, "E274", {"start": v(987.04, 68.98) * mm, "mid": v(987.15, 68.87) * mm, "end": v(987.19, 68.72) * mm});
            skLineSegment(sketch, "E275", {"start": v(987.19, 68.72) * mm, "end": v(987.19, 68.36) * mm});
            skArc(sketch, "E276", {"start": v(987.19, 68.36) * mm, "mid": v(987.15, 68.21) * mm, "end": v(987.04, 68.1) * mm});
            skLineSegment(sketch, "E277", {"start": v(987.04, 68.1) * mm, "end": v(986.89, 68.01) * mm});
            skArc(sketch, "E278", {"start": v(986.89, 68.01) * mm, "mid": v(986.79, 67.84) * mm, "end": v(986.89, 67.67) * mm});
            skLineSegment(sketch, "E279", {"start": v(986.89, 67.67) * mm, "end": v(987.06, 67.57) * mm});
            skArc(sketch, "E280", {"start": v(987.06, 67.57) * mm, "mid": v(987.16, 67.48) * mm, "end": v(987.2, 67.35) * mm});
            skLineSegment(sketch, "E281", {"start": v(0, 0) * mm, "end": v(0, 95.02) * mm, "construction": true});
            skArc(sketch, "E282", {"start": v(1033.41, 83.26) * mm, "mid": v(1033.33, 83.05) * mm, "end": v(1033.11, 82.96) * mm});
            skLineSegment(sketch, "E283", {"start": v(1033.11, 82.96) * mm, "end": v(1029.41, 82.96) * mm});
            skArc(sketch, "E284", {"start": v(1029.41, 82.96) * mm, "mid": v(1029.2, 83.05) * mm, "end": v(1029.11, 83.26) * mm});
            skLineSegment(sketch, "E285", {"start": v(1029.11, 83.26) * mm, "end": v(1029.11, 85.47) * mm});
            skArc(sketch, "E286", {"start": v(1029.11, 85.47) * mm, "mid": v(1029.18, 85.66) * mm, "end": v(1029.35, 85.76) * mm});
            skLineSegment(sketch, "E287", {"start": v(1029.35, 85.76) * mm, "end": v(1031.26, 86.16) * mm});
            skLineSegment(sketch, "E288", {"start": v(1031.26, 86.16) * mm, "end": v(1033.18, 85.76) * mm});
            skArc(sketch, "E289", {"start": v(1033.18, 85.76) * mm, "mid": v(1033.35, 85.66) * mm, "end": v(1033.41, 85.47) * mm});
            skLineSegment(sketch, "E290", {"start": v(1033.41, 85.47) * mm, "end": v(1033.41, 83.26) * mm});
            skArc(sketch, "E291", {"start": v(1028.57, 79.76) * mm, "mid": v(1028.88, 79.82) * mm, "end": v(1029.14, 80) * mm});
            skLineSegment(sketch, "E292", {"start": v(1029.14, 80) * mm, "end": v(1029.52, 80.37) * mm});
            skArc(sketch, "E293", {"start": v(1029.52, 80.37) * mm, "mid": v(1029.61, 80.44) * mm, "end": v(1029.73, 80.46) * mm});
            skLineSegment(sketch, "E294", {"start": v(1029.73, 80.46) * mm, "end": v(1032.8, 80.46) * mm});
            skArc(sketch, "E295", {"start": v(1032.8, 80.46) * mm, "mid": v(1032.92, 80.44) * mm, "end": v(1033.01, 80.37) * mm});
            skLineSegment(sketch, "E296", {"start": v(1033.01, 80.37) * mm, "end": v(1033.4, 80) * mm});
            skArc(sketch, "E297", {"start": v(1033.4, 80) * mm, "mid": v(1033.65, 79.82) * mm, "end": v(1033.96, 79.76) * mm});
            skLineSegment(sketch, "E298", {"start": v(1033.96, 79.76) * mm, "end": v(1034.61, 79.76) * mm});
            skLineSegment(sketch, "E299", {"start": v(1034.61, 79.76) * mm, "end": v(1034.91, 80) * mm});
            skLineSegment(sketch, "E300", {"start": v(1034.91, 80) * mm, "end": v(1034.61, 80.26) * mm});
            skLineSegment(sketch, "E301", {"start": v(1034.61, 80.26) * mm, "end": v(1033.96, 80.26) * mm});
            skArc(sketch, "E302", {"start": v(1033.96, 80.26) * mm, "mid": v(1033.84, 80.28) * mm, "end": v(1033.74, 80.35) * mm});
            skLineSegment(sketch, "E303", {"start": v(1033.74, 80.35) * mm, "end": v(1033.37, 80.73) * mm});
            skArc(sketch, "E304", {"start": v(1033.37, 80.73) * mm, "mid": v(1033.1, 80.9) * mm, "end": v(1032.8, 80.96) * mm});
            skLineSegment(sketch, "E305", {"start": v(1032.8, 80.96) * mm, "end": v(1032.7, 80.6) * mm});
            skArc(sketch, "E306", {"start": v(1032.7, 80.6) * mm, "mid": v(1032.51, 80.46) * mm, "end": v(1032.32, 80.6) * mm});
            skLineSegment(sketch, "E307", {"start": v(1032.32, 80.6) * mm, "end": v(1032.23, 80.96) * mm});
            skLineSegment(sketch, "E308", {"start": v(1032.23, 80.96) * mm, "end": v(1030.3, 80.96) * mm});
            skLineSegment(sketch, "E309", {"start": v(1030.3, 80.96) * mm, "end": v(1030.2, 80.6) * mm});
            skArc(sketch, "E310", {"start": v(1030.2, 80.6) * mm, "mid": v(1030.02, 80.46) * mm, "end": v(1029.82, 80.6) * mm});
            skLineSegment(sketch, "E311", {"start": v(1029.82, 80.6) * mm, "end": v(1029.73, 80.96) * mm});
            skArc(sketch, "E312", {"start": v(1029.73, 80.96) * mm, "mid": v(1029.42, 80.9) * mm, "end": v(1029.16, 80.73) * mm});
            skLineSegment(sketch, "E313", {"start": v(1029.16, 80.73) * mm, "end": v(1028.79, 80.35) * mm});
            skArc(sketch, "E314", {"start": v(1028.79, 80.35) * mm, "mid": v(1028.69, 80.28) * mm, "end": v(1028.57, 80.26) * mm});
            skLineSegment(sketch, "E315", {"start": v(1028.57, 80.26) * mm, "end": v(1027.9, 80.26) * mm});
            skLineSegment(sketch, "E316", {"start": v(1027.9, 80.26) * mm, "end": v(1027.8, 79.9) * mm});
            skArc(sketch, "E317", {"start": v(1027.8, 79.9) * mm, "mid": v(1027.61, 79.76) * mm, "end": v(1027.42, 79.9) * mm});
            skLineSegment(sketch, "E318", {"start": v(1027.42, 79.9) * mm, "end": v(1027.33, 80.26) * mm});
            skLineSegment(sketch, "E319", {"start": v(1027.33, 80.26) * mm, "end": v(1026.81, 80.26) * mm});
            skArc(sketch, "E320", {"start": v(1026.81, 80.26) * mm, "mid": v(1026.6, 80.35) * mm, "end": v(1026.51, 80.56) * mm});
            skLineSegment(sketch, "E321", {"start": v(1026.51, 80.56) * mm, "end": v(1026.51, 87.7) * mm});
            skLineSegment(sketch, "E322", {"start": v(1026.51, 87.7) * mm, "end": v(1026.02, 90.26) * mm});
            skArc(sketch, "E323", {"start": v(1026.02, 90.26) * mm, "mid": v(1026.18, 90.54) * mm, "end": v(1026.48, 90.43) * mm});
            skLineSegment(sketch, "E324", {"start": v(1026.48, 90.43) * mm, "end": v(1028.28, 87.23) * mm});
            skArc(sketch, "E325", {"start": v(1028.28, 87.23) * mm, "mid": v(1028.42, 87.17) * mm, "end": v(1028.5, 87.29) * mm});
            skLineSegment(sketch, "E326", {"start": v(1028.5, 87.29) * mm, "end": v(1028.48, 88.98) * mm});
            skArc(sketch, "E327", {"start": v(1028.48, 88.98) * mm, "mid": v(1028.67, 89.23) * mm, "end": v(1028.95, 89.1) * mm});
            skLineSegment(sketch, "E328", {"start": v(1028.95, 89.1) * mm, "end": v(1029.6, 87.9) * mm});
            skLineSegment(sketch, "E329", {"start": v(1029.6, 87.9) * mm, "end": v(1029.74, 89.26) * mm});
            skArc(sketch, "E330", {"start": v(1029.74, 89.26) * mm, "mid": v(1029.96, 89.48) * mm, "end": v(1030.22, 89.32) * mm});
            skLineSegment(sketch, "E331", {"start": v(1030.22, 89.32) * mm, "end": v(1030.7, 88.04) * mm});
            skLineSegment(sketch, "E332", {"start": v(1030.7, 88.04) * mm, "end": v(1031.02, 89.37) * mm});
            skArc(sketch, "E333", {"start": v(1031.02, 89.37) * mm, "mid": v(1031.26, 89.56) * mm, "end": v(1031.5, 89.37) * mm});
            skLineSegment(sketch, "E334", {"start": v(1031.5, 89.37) * mm, "end": v(1031.83, 88.04) * mm});
            skLineSegment(sketch, "E335", {"start": v(1031.83, 88.04) * mm, "end": v(1032.3, 89.32) * mm});
            skArc(sketch, "E336", {"start": v(1032.3, 89.32) * mm, "mid": v(1032.57, 89.48) * mm, "end": v(1032.8, 89.26) * mm});
            skLineSegment(sketch, "E337", {"start": v(1032.8, 89.26) * mm, "end": v(1032.94, 87.9) * mm});
            skLineSegment(sketch, "E338", {"start": v(1032.94, 87.9) * mm, "end": v(1033.58, 89.1) * mm});
            skArc(sketch, "E339", {"start": v(1033.58, 89.1) * mm, "mid": v(1033.86, 89.23) * mm, "end": v(1034.05, 88.98) * mm});
            skLineSegment(sketch, "E340", {"start": v(1034.05, 88.98) * mm, "end": v(1034.02, 87.29) * mm});
            skArc(sketch, "E341", {"start": v(1034.02, 87.29) * mm, "mid": v(1034.1, 87.17) * mm, "end": v(1034.25, 87.23) * mm});
            skLineSegment(sketch, "E342", {"start": v(1034.25, 87.23) * mm, "end": v(1036.05, 90.43) * mm});
            skArc(sketch, "E343", {"start": v(1036.05, 90.43) * mm, "mid": v(1036.35, 90.54) * mm, "end": v(1036.51, 90.26) * mm});
            skLineSegment(sketch, "E344", {"start": v(1036.51, 90.26) * mm, "end": v(1036.01, 87.7) * mm});
            skLineSegment(sketch, "E345", {"start": v(1036.01, 87.7) * mm, "end": v(1036.01, 80.26) * mm});
            skLineSegment(sketch, "E346", {"start": v(1036.01, 80.26) * mm, "end": v(1035.71, 80) * mm});
            skLineSegment(sketch, "E347", {"start": v(1035.71, 80) * mm, "end": v(1036.01, 79.76) * mm});
            skLineSegment(sketch, "E348", {"start": v(1036.01, 79.76) * mm, "end": v(1036.01, 79.36) * mm});
            skArc(sketch, "E349", {"start": v(1036.01, 79.36) * mm, "mid": v(1035.93, 79.15) * mm, "end": v(1035.71, 79.06) * mm});
            skLineSegment(sketch, "E350", {"start": v(1035.71, 79) * mm, "end": v(1034.16, 79) * mm});
            skLineSegment(sketch, "E351", {"start": v(1034.16, 79.06) * mm, "end": v(1033.33, 79.25) * mm});
            skArc(sketch, "E352", {"start": v(1033.33, 79.25) * mm, "mid": v(1033.08, 79.2) * mm, "end": v(1032.96, 78.96) * mm});
            skLineSegment(sketch, "E353", {"start": v(1032.96, 77.76) * mm, "end": v(1033.26, 77.76) * mm});
            skArc(sketch, "E354", {"start": v(1033.26, 77.76) * mm, "mid": v(1033.54, 77.58) * mm, "end": v(1033.48, 77.25) * mm});
            skLineSegment(sketch, "E355", {"start": v(1033.48, 77.25) * mm, "end": v(1032.4, 76.15) * mm});
            skArc(sketch, "E356", {"start": v(1032.4, 76.15) * mm, "mid": v(1032.3, 76.08) * mm, "end": v(1032.19, 76.06) * mm});
            skLineSegment(sketch, "E357", {"start": v(1032.19, 76.06) * mm, "end": v(1030.34, 76.06) * mm});
            skArc(sketch, "E358", {"start": v(1030.34, 76.06) * mm, "mid": v(1030.23, 76.08) * mm, "end": v(1030.13, 76.15) * mm});
            skLineSegment(sketch, "E359", {"start": v(1030.13, 76.15) * mm, "end": v(1029.05, 77.25) * mm});
            skArc(sketch, "E360", {"start": v(1029.05, 77.25) * mm, "mid": v(1028.99, 77.58) * mm, "end": v(1029.26, 77.76) * mm});
            skLineSegment(sketch, "E361", {"start": v(1029.26, 77.76) * mm, "end": v(1029.56, 77.76) * mm});
            skArc(sketch, "E362", {"start": v(1029.56, 78.96) * mm, "mid": v(1029.45, 79.2) * mm, "end": v(1029.2, 79.25) * mm});
            skLineSegment(sketch, "E363", {"start": v(1029.2, 79.25) * mm, "end": v(1028.36, 79.06) * mm});
            skLineSegment(sketch, "E364", {"start": v(1028.36, 79.06) * mm, "end": v(1026.86, 79.06) * mm});
            skArc(sketch, "E365", {"start": v(1026.86, 79.06) * mm, "mid": v(1026.51, 79.4) * mm, "end": v(1026.86, 79.76) * mm});
            skLineSegment(sketch, "E366", {"start": v(1026.86, 79.76) * mm, "end": v(1028.57, 79.76) * mm});
            skArc(sketch, "E367", {"start": v(1030.51, 77.16) * mm, "mid": v(1030.6, 76.95) * mm, "end": v(1030.81, 76.86) * mm});
            skLineSegment(sketch, "E368", {"start": v(1030.81, 76.86) * mm, "end": v(1031.71, 76.86) * mm});
            skArc(sketch, "E369", {"start": v(1031.71, 76.86) * mm, "mid": v(1031.93, 76.95) * mm, "end": v(1032.01, 77.16) * mm});
            skLineSegment(sketch, "E370", {"start": v(1032.01, 77.16) * mm, "end": v(1032.01, 78.76) * mm});
            skArc(sketch, "E371", {"start": v(1032.01, 78.76) * mm, "mid": v(1031.93, 78.97) * mm, "end": v(1031.71, 79.06) * mm});
            skLineSegment(sketch, "E372", {"start": v(1031.71, 79.06) * mm, "end": v(1030.81, 79.06) * mm});
            skArc(sketch, "E373", {"start": v(1030.81, 79.06) * mm, "mid": v(1030.6, 78.97) * mm, "end": v(1030.51, 78.76) * mm});
            skLineSegment(sketch, "E374", {"start": v(1030.51, 78.76) * mm, "end": v(1030.51, 77.16) * mm});
            skLineSegment(sketch, "E375", {"start": v(1010, 66) * mm, "end": v(1010, 105.34) * mm, "construction": true});
            skLineSegment(sketch, "E376.MirrorCS", {"start": v(986.9, 75.01) * mm, "end": v(987.04, 75.1) * mm});
            skLineSegment(sketch, "E377.MirrorCS", {"start": v(990.31, 78.5) * mm, "end": v(990.31, 78) * mm});
            skLineSegment(sketch, "E378.MirrorCS", {"start": v(990.81, 79) * mm, "end": v(990.31, 78.5) * mm});
            skArc(sketch, "E379.MirrorCS", {"start": v(986.89, 74.67) * mm, "mid": v(986.8, 74.84) * mm, "end": v(986.89, 75.01) * mm});
            skArc(sketch, "E380.MirrorCS", {"start": v(987.04, 75.1) * mm, "mid": v(987.15, 75.21) * mm, "end": v(987.2, 75.36) * mm});
            skLineSegment(sketch, "E381.MirrorCS", {"start": v(987.2, 78) * mm, "end": v(987.2, 78.5) * mm});
            skLineSegment(sketch, "E382.MirrorCS", {"start": v(987.2, 78.5) * mm, "end": v(986.7, 79) * mm});
            skLineSegment(sketch, "E383.MirrorCS", {"start": v(991.31, 78) * mm, "end": v(991.31, 77.07) * mm});
            skLineSegment(sketch, "E384.MirrorCS", {"start": v(990.31, 78) * mm, "end": v(991.31, 78) * mm});
            skLineSegment(sketch, "E385.MirrorCS", {"start": v(990.46, 75.8) * mm, "end": v(990.61, 75.71) * mm});
            skLineSegment(sketch, "E386.MirrorCS", {"start": v(990.31, 75.02) * mm, "end": v(990.31, 74.66) * mm});
            skArc(sketch, "E387.MirrorCS", {"start": v(990.46, 75.28) * mm, "mid": v(990.35, 75.17) * mm, "end": v(990.31, 75.02) * mm});
            skLineSegment(sketch, "E388.MirrorCS", {"start": v(986.2, 78) * mm, "end": v(987.2, 78) * mm});
            skArc(sketch, "E389.MirrorCS", {"start": v(990.61, 75.71) * mm, "mid": v(990.71, 75.54) * mm, "end": v(990.61, 75.37) * mm});
            skArc(sketch, "E390.MirrorCS", {"start": v(990.31, 76.07) * mm, "mid": v(990.35, 75.91) * mm, "end": v(990.46, 75.8) * mm});
            skLineSegment(sketch, "E391.MirrorCS", {"start": v(990.61, 75.37) * mm, "end": v(990.46, 75.28) * mm});
            skLineSegment(sketch, "E392.MirrorCS", {"start": v(991.64, 79) * mm, "end": v(993.14, 79) * mm});
            skLineSegment(sketch, "E393.MirrorCS", {"start": v(984.29, 79) * mm, "end": v(985.84, 79) * mm});
            skLineSegment(sketch, "E394.MirrorCS", {"start": v(991.31, 77.07) * mm, "end": v(990.31, 76.07) * mm});
            skLineSegment(sketch, "E395.MirrorCS", {"start": v(986.2, 77.07) * mm, "end": v(986.2, 78) * mm});
            skLineSegment(sketch, "E396.MirrorCS", {"start": v(987.2, 75.36) * mm, "end": v(987.2, 76.07) * mm});
            skLineSegment(sketch, "E397.MirrorCS", {"start": v(986.7, 79) * mm, "end": v(984, 79) * mm});
            skLineSegment(sketch, "E398.MirrorCS", {"start": v(987.2, 76.07) * mm, "end": v(986.19, 77.07) * mm});
            skLineSegment(sketch, "E399.MirrorCS", {"start": v(993.5, 79) * mm, "end": v(990.81, 79) * mm});
            skLineSegment(sketch, "E400.MirrorCS", {"start": v(993.5, 67) * mm, "end": v(993.5, 79) * mm});
            skLineSegment(sketch, "E401.MirrorCS", {"start": v(984, 79) * mm, "end": v(984, 14.5) * mm});
            skLineSegment(sketch, "E402", {"start": v(1034.16, 79.06) * mm, "end": v(1035.71, 79.06) * mm});
            skArc(sketch, "E403", {"start": v(1029.56, 77.76) * mm, "mid": v(1029.8, 78.36) * mm, "end": v(1029.56, 78.96) * mm});
            skArc(sketch, "E404", {"start": v(1032.96, 78.96) * mm, "mid": v(1032.7, 78.36) * mm, "end": v(1032.96, 77.76) * mm});
            skLineSegment(sketch, "E405.MirrorCS", {"start": v(987.99, 77.16) * mm, "end": v(987.99, 78.76) * mm});
            skArc(sketch, "E406.MirrorCS", {"start": v(987.99, 78.76) * mm, "mid": v(988.07, 78.97) * mm, "end": v(988.29, 79.06) * mm});
            skArc(sketch, "E407.MirrorCS", {"start": v(987.04, 78.96) * mm, "mid": v(987.3, 78.36) * mm, "end": v(987.04, 77.76) * mm});
            skLineSegment(sketch, "E408.MirrorCS", {"start": v(986.26, 80.35) * mm, "end": v(986.63, 80.73) * mm});
            skLineSegment(sketch, "E409.MirrorCS", {"start": v(986.99, 80.37) * mm, "end": v(986.6, 80) * mm});
            skArc(sketch, "E410.MirrorCS", {"start": v(986.04, 80.26) * mm, "mid": v(986.16, 80.28) * mm, "end": v(986.26, 80.35) * mm});
            skArc(sketch, "E411.MirrorCS", {"start": v(983.99, 79.36) * mm, "mid": v(984.07, 79.15) * mm, "end": v(984.29, 79.06) * mm});
            skLineSegment(sketch, "E412.MirrorCS", {"start": v(985.84, 79.06) * mm, "end": v(986.67, 79.25) * mm});
            skArc(sketch, "E413.MirrorCS", {"start": v(991.21, 80.35) * mm, "mid": v(991.31, 80.28) * mm, "end": v(991.43, 80.26) * mm});
            skArc(sketch, "E414.MirrorCS", {"start": v(986.67, 79.25) * mm, "mid": v(986.92, 79.2) * mm, "end": v(987.04, 78.96) * mm});
            skLineSegment(sketch, "E415.MirrorCS", {"start": v(992.67, 80.26) * mm, "end": v(993.19, 80.26) * mm});
            skLineSegment(sketch, "E416.MirrorCS", {"start": v(992.58, 79.9) * mm, "end": v(992.67, 80.26) * mm});
            skArc(sketch, "E417.MirrorCS", {"start": v(993.19, 80.26) * mm, "mid": v(993.4, 80.35) * mm, "end": v(993.49, 80.56) * mm});
            skArc(sketch, "E418.MirrorCS", {"start": v(987.2, 80.46) * mm, "mid": v(987.08, 80.44) * mm, "end": v(986.99, 80.37) * mm});
            skArc(sketch, "E419.MirrorCS", {"start": v(990.44, 78.96) * mm, "mid": v(990.55, 79.2) * mm, "end": v(990.8, 79.25) * mm});
            skLineSegment(sketch, "E420.MirrorCS", {"start": v(991.43, 80.26) * mm, "end": v(992.1, 80.26) * mm});
            skLineSegment(sketch, "E421.MirrorCS", {"start": v(987.68, 80.6) * mm, "end": v(987.77, 80.96) * mm});
            skArc(sketch, "E422.MirrorCS", {"start": v(990.26, 89.26) * mm, "mid": v(990.04, 89.48) * mm, "end": v(989.78, 89.32) * mm});
            skLineSegment(sketch, "E423.MirrorCS", {"start": v(983.99, 80.26) * mm, "end": v(984.29, 80) * mm});
            skLineSegment(sketch, "E424.MirrorCS", {"start": v(986.04, 79.76) * mm, "end": v(985.39, 79.76) * mm});
            skArc(sketch, "E425.MirrorCS", {"start": v(990.59, 82.96) * mm, "mid": v(990.8, 83.05) * mm, "end": v(990.89, 83.26) * mm});
            skLineSegment(sketch, "E426.MirrorCS", {"start": v(984.29, 80) * mm, "end": v(983.99, 79.76) * mm});
            skArc(sketch, "E427.MirrorCS", {"start": v(987.7, 89.32) * mm, "mid": v(987.43, 89.48) * mm, "end": v(987.2, 89.26) * mm});
            skArc(sketch, "E428.MirrorCS", {"start": v(989.8, 80.6) * mm, "mid": v(989.98, 80.46) * mm, "end": v(990.18, 80.6) * mm});
            skArc(sketch, "E429.MirrorCS", {"start": v(986.82, 85.76) * mm, "mid": v(986.65, 85.66) * mm, "end": v(986.59, 85.47) * mm});
            skLineSegment(sketch, "E430.MirrorCS", {"start": v(983.99, 79.76) * mm, "end": v(983.99, 79.36) * mm});
            skLineSegment(sketch, "E431.MirrorCS", {"start": v(990.8, 79.25) * mm, "end": v(991.64, 79.06) * mm});
            skArc(sketch, "E432.MirrorCS", {"start": v(986.63, 80.73) * mm, "mid": v(986.9, 80.9) * mm, "end": v(987.2, 80.96) * mm});
            skArc(sketch, "E433.MirrorCS", {"start": v(993.14, 79.06) * mm, "mid": v(993.49, 79.4) * mm, "end": v(993.14, 79.76) * mm});
            skLineSegment(sketch, "E434.MirrorCS", {"start": v(985.39, 79.76) * mm, "end": v(985.09, 80) * mm});
            skArc(sketch, "E435.MirrorCS", {"start": v(983.95, 90.43) * mm, "mid": v(983.65, 90.54) * mm, "end": v(983.49, 90.26) * mm});
            skLineSegment(sketch, "E436.MirrorCS", {"start": v(987.2, 80.96) * mm, "end": v(987.3, 80.6) * mm});
            skArc(sketch, "E437.MirrorCS", {"start": v(986.6, 80) * mm, "mid": v(986.35, 79.82) * mm, "end": v(986.04, 79.76) * mm});
            skArc(sketch, "E438.MirrorCS", {"start": v(987.3, 80.6) * mm, "mid": v(987.49, 80.46) * mm, "end": v(987.68, 80.6) * mm});
            skLineSegment(sketch, "E439.MirrorCS", {"start": v(989.49, 78.76) * mm, "end": v(989.49, 77.16) * mm});
            skArc(sketch, "E440.MirrorCS", {"start": v(992.2, 79.9) * mm, "mid": v(992.39, 79.76) * mm, "end": v(992.58, 79.9) * mm});
            skArc(sketch, "E441.MirrorCS", {"start": v(989.19, 79.06) * mm, "mid": v(989.4, 78.97) * mm, "end": v(989.49, 78.76) * mm});
            skLineSegment(sketch, "E442.MirrorCS", {"start": v(988.29, 79.06) * mm, "end": v(989.19, 79.06) * mm});
            skLineSegment(sketch, "E443.MirrorCS", {"start": v(990.84, 80.73) * mm, "end": v(991.21, 80.35) * mm});
            skArc(sketch, "E444.MirrorCS", {"start": v(990.89, 85.47) * mm, "mid": v(990.82, 85.66) * mm, "end": v(990.65, 85.76) * mm});
            skArc(sketch, "E445.MirrorCS", {"start": v(991.72, 87.23) * mm, "mid": v(991.58, 87.17) * mm, "end": v(991.5, 87.29) * mm});
            skLineSegment(sketch, "E446.MirrorCS", {"start": v(993.14, 79.76) * mm, "end": v(991.43, 79.76) * mm});
            skArc(sketch, "E447.MirrorCS", {"start": v(986.59, 83.26) * mm, "mid": v(986.67, 83.05) * mm, "end": v(986.89, 82.96) * mm});
            skArc(sketch, "E448.MirrorCS", {"start": v(991.43, 79.76) * mm, "mid": v(991.12, 79.82) * mm, "end": v(990.86, 80) * mm});
            skLineSegment(sketch, "E449.MirrorCS", {"start": v(985.09, 80) * mm, "end": v(985.39, 80.26) * mm});
            skArc(sketch, "E450.MirrorCS", {"start": v(988.98, 89.37) * mm, "mid": v(988.74, 89.56) * mm, "end": v(988.5, 89.37) * mm});
            skArc(sketch, "E451.MirrorCS", {"start": v(990.44, 77.76) * mm, "mid": v(990.2, 78.36) * mm, "end": v(990.44, 78.96) * mm});
            skArc(sketch, "E452.MirrorCS", {"start": v(990.48, 80.37) * mm, "mid": v(990.39, 80.44) * mm, "end": v(990.27, 80.46) * mm});
            skArc(sketch, "E453.MirrorCS", {"start": v(986.42, 89.1) * mm, "mid": v(986.14, 89.23) * mm, "end": v(985.95, 88.98) * mm});
            skLineSegment(sketch, "E454.MirrorCS", {"start": v(990.18, 80.6) * mm, "end": v(990.27, 80.96) * mm});
            skLineSegment(sketch, "E455.MirrorCS", {"start": v(990.86, 80) * mm, "end": v(990.48, 80.37) * mm});
            skArc(sketch, "E456.MirrorCS", {"start": v(990.27, 80.96) * mm, "mid": v(990.58, 80.9) * mm, "end": v(990.84, 80.73) * mm});
            skArc(sketch, "E457.MirrorCS", {"start": v(993.98, 90.26) * mm, "mid": v(993.82, 90.54) * mm, "end": v(993.52, 90.43) * mm});
            skLineSegment(sketch, "E458.MirrorCS", {"start": v(989.7, 80.96) * mm, "end": v(989.8, 80.6) * mm});
            skArc(sketch, "E459.MirrorCS", {"start": v(991.52, 88.98) * mm, "mid": v(991.33, 89.23) * mm, "end": v(991.05, 89.1) * mm});
            skLineSegment(sketch, "E460.MirrorCS", {"start": v(992.1, 80.26) * mm, "end": v(992.2, 79.9) * mm});
            skLineSegment(sketch, "E461.MirrorCS", {"start": v(985.39, 80.26) * mm, "end": v(986.04, 80.26) * mm});
            skArc(sketch, "E462.MirrorCS", {"start": v(985.98, 87.29) * mm, "mid": v(985.9, 87.17) * mm, "end": v(985.75, 87.23) * mm});
            skLineSegment(sketch, "E463.MirrorCS", {"start": v(988.5, 89.37) * mm, "end": v(988.17, 88.04) * mm});
            skLineSegment(sketch, "E464.MirrorCS", {"start": v(991.05, 89.1) * mm, "end": v(990.4, 87.9) * mm});
            skLineSegment(sketch, "E465.MirrorCS", {"start": v(990.27, 80.46) * mm, "end": v(987.2, 80.46) * mm});
            skLineSegment(sketch, "E466.MirrorCS", {"start": v(990.89, 83.26) * mm, "end": v(990.89, 85.47) * mm});
            skLineSegment(sketch, "E467.MirrorCS", {"start": v(990.65, 85.76) * mm, "end": v(988.74, 86.16) * mm});
            skLineSegment(sketch, "E468.MirrorCS", {"start": v(991.64, 79.06) * mm, "end": v(993.14, 79.06) * mm});
            skLineSegment(sketch, "E469.MirrorCS", {"start": v(987.06, 87.9) * mm, "end": v(986.42, 89.1) * mm});
            skLineSegment(sketch, "E470.MirrorCS", {"start": v(991.5, 87.29) * mm, "end": v(991.52, 88.98) * mm});
            skLineSegment(sketch, "E471.MirrorCS", {"start": v(990.4, 87.9) * mm, "end": v(990.26, 89.26) * mm});
            skLineSegment(sketch, "E472.MirrorCS", {"start": v(993.49, 80.56) * mm, "end": v(993.49, 87.7) * mm});
            skLineSegment(sketch, "E473.MirrorCS", {"start": v(985.84, 79.06) * mm, "end": v(984.29, 79.06) * mm});
            skLineSegment(sketch, "E474.MirrorCS", {"start": v(987.77, 80.96) * mm, "end": v(989.7, 80.96) * mm});
            skLineSegment(sketch, "E475.MirrorCS", {"start": v(986.89, 82.96) * mm, "end": v(990.59, 82.96) * mm});
            skLineSegment(sketch, "E476.MirrorCS", {"start": v(986.59, 85.47) * mm, "end": v(986.59, 83.26) * mm});
            skLineSegment(sketch, "E477.MirrorCS", {"start": v(985.95, 88.98) * mm, "end": v(985.98, 87.29) * mm});
            skLineSegment(sketch, "E478.MirrorCS", {"start": v(993.52, 90.43) * mm, "end": v(991.72, 87.23) * mm});
            skLineSegment(sketch, "E479.MirrorCS", {"start": v(983.49, 90.26) * mm, "end": v(983.99, 87.7) * mm});
            skLineSegment(sketch, "E480.MirrorCS", {"start": v(983.99, 87.7) * mm, "end": v(983.99, 80.26) * mm});
            skLineSegment(sketch, "E481.MirrorCS", {"start": v(989.78, 89.32) * mm, "end": v(989.3, 88.04) * mm});
            skLineSegment(sketch, "E482.MirrorCS", {"start": v(988.17, 88.04) * mm, "end": v(987.7, 89.32) * mm});
            skLineSegment(sketch, "E483.MirrorCS", {"start": v(993.49, 87.7) * mm, "end": v(993.98, 90.26) * mm});
            skLineSegment(sketch, "E484.MirrorCS", {"start": v(988.74, 86.16) * mm, "end": v(986.82, 85.76) * mm});
            skLineSegment(sketch, "E485.MirrorCS", {"start": v(989.3, 88.04) * mm, "end": v(988.98, 89.37) * mm});
            skLineSegment(sketch, "E486.MirrorCS", {"start": v(987.2, 89.26) * mm, "end": v(987.06, 87.9) * mm});
            skLineSegment(sketch, "E487.MirrorCS", {"start": v(985.75, 87.23) * mm, "end": v(983.95, 90.43) * mm});
            skLineSegment(sketch, "E488.MirrorCS", {"start": v(990.46, 74.4) * mm, "end": v(990.61, 74.31) * mm});
            skArc(sketch, "E489.MirrorCS", {"start": v(990.31, 74.66) * mm, "mid": v(990.35, 74.51) * mm, "end": v(990.46, 74.4) * mm});
            skLineSegment(sketch, "E490.MirrorCS", {"start": v(990.61, 73.97) * mm, "end": v(990.46, 73.88) * mm});
            skLineSegment(sketch, "E491.MirrorCS", {"start": v(990.74, 77.76) * mm, "end": v(990.44, 77.76) * mm});
            skArc(sketch, "E492.MirrorCS", {"start": v(989.49, 77.16) * mm, "mid": v(989.4, 76.95) * mm, "end": v(989.19, 76.86) * mm});
            skLineSegment(sketch, "E493.MirrorCS", {"start": v(987.04, 74.58) * mm, "end": v(986.9, 74.67) * mm});
            skArc(sketch, "E494.MirrorCS", {"start": v(990.95, 77.25) * mm, "mid": v(991.01, 77.58) * mm, "end": v(990.74, 77.76) * mm});
            skArc(sketch, "E495.MirrorCS", {"start": v(990.61, 74.31) * mm, "mid": v(990.71, 74.14) * mm, "end": v(990.61, 73.97) * mm});
            skLineSegment(sketch, "E496.MirrorCS", {"start": v(987.04, 77.76) * mm, "end": v(986.74, 77.76) * mm});
            skArc(sketch, "E497.MirrorCS", {"start": v(987.04, 73.7) * mm, "mid": v(987.15, 73.81) * mm, "end": v(987.2, 73.96) * mm});
            skLineSegment(sketch, "E498.MirrorCS", {"start": v(987.2, 73.96) * mm, "end": v(987.2, 74.32) * mm});
            skArc(sketch, "E499.MirrorCS", {"start": v(987.2, 74.32) * mm, "mid": v(987.15, 74.47) * mm, "end": v(987.04, 74.58) * mm});
            skArc(sketch, "E500.MirrorCS", {"start": v(989.66, 76.06) * mm, "mid": v(989.77, 76.08) * mm, "end": v(989.87, 76.15) * mm});
            skArc(sketch, "E501.MirrorCS", {"start": v(988.29, 76.86) * mm, "mid": v(988.07, 76.95) * mm, "end": v(987.99, 77.16) * mm});
            skArc(sketch, "E502.MirrorCS", {"start": v(987.6, 76.15) * mm, "mid": v(987.7, 76.08) * mm, "end": v(987.81, 76.06) * mm});
            skArc(sketch, "E503.MirrorCS", {"start": v(986.74, 77.76) * mm, "mid": v(986.46, 77.58) * mm, "end": v(986.52, 77.25) * mm});
            skLineSegment(sketch, "E504.MirrorCS", {"start": v(989.19, 76.86) * mm, "end": v(988.29, 76.86) * mm});
            skLineSegment(sketch, "E505.MirrorCS", {"start": v(986.52, 77.25) * mm, "end": v(987.6, 76.15) * mm});
            skLineSegment(sketch, "E506.MirrorCS", {"start": v(989.87, 76.15) * mm, "end": v(990.95, 77.25) * mm});
            skLineSegment(sketch, "E507.MirrorCS", {"start": v(987.81, 76.06) * mm, "end": v(989.66, 76.06) * mm});
            skSolve(sketch);
        }
        {
            var Q0;
            Q0=makeQuery(id+"F5.imprint","IMPRINT",FACE,{"disambiguationData":[TD([[makeQuery(id+"F5.imprint","IMPRINT",EDGE,{"derivedFrom":sQuery(id+"F5.wireOp",EDGE,"E8")}),-1.0]])]});
            var Q1;
            Q1=sQuery(id+"F5.wireOp",EDGE,"E281");
            revolve(context, id + "F6", {"surfaceOperationType" : NewSurfaceOperationType.NEW, "entities" : qUnion([Q0]), "axis" : qUnion([Q1]), "revolveType" : RevolveType.ONE_DIRECTION, "oppositeDirection" : true, "angle" : 179.8 * degree});
        }
    });
